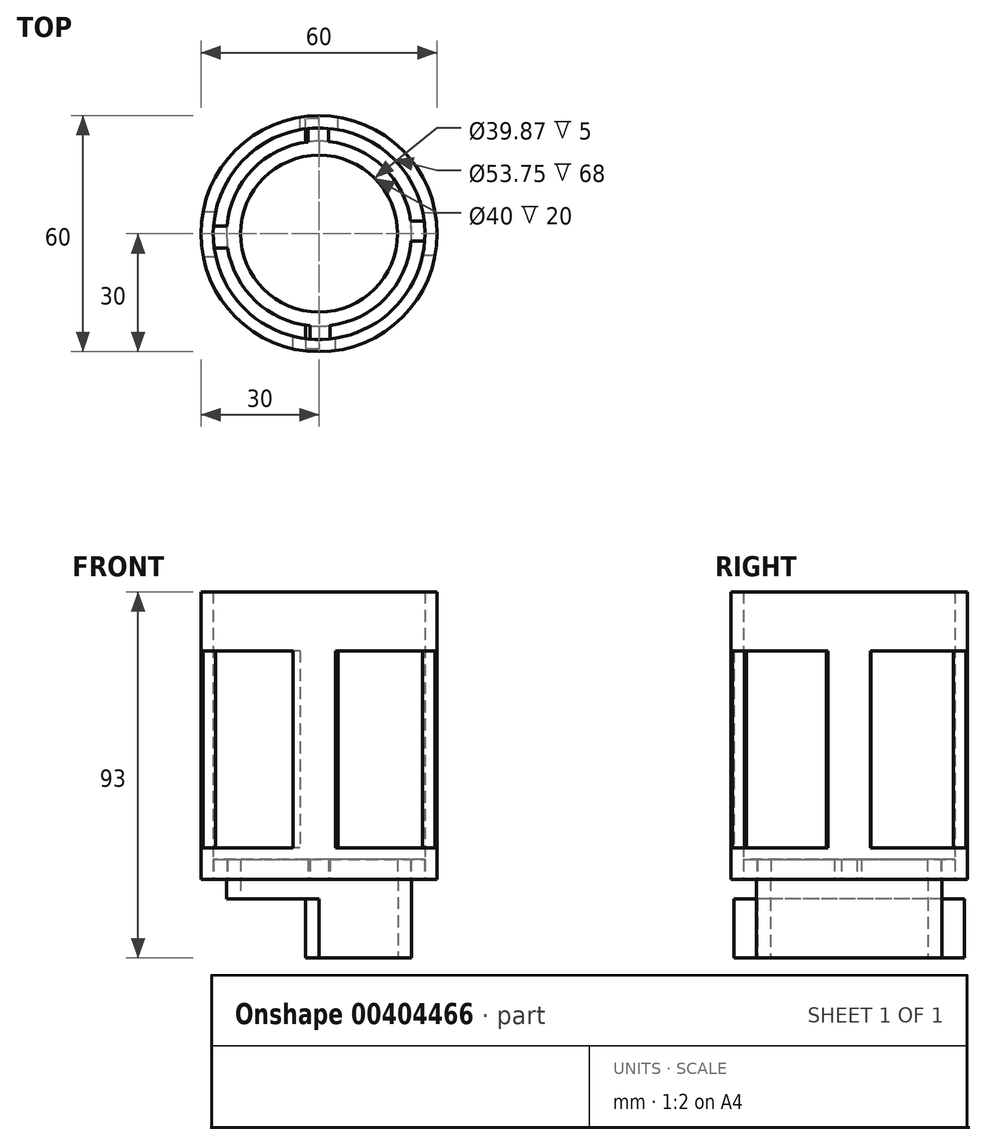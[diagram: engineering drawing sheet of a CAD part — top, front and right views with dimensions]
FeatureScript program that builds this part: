
annotation { "Feature Type Name" : "Feature", "Feature Type Description" : "" }
export const myFeature = defineFeature(function(context is Context, id is Id, definition is map)
    precondition{}
    {
        {
            var Q0;
            Q0=qCreatedBy(makeId("Top.planeOp"),FACE);
            var sketch = newSketch(context, id + "F0", { "sketchPlane" : qUnion([Q0])});
            skCircle(sketch, "E0", {"center": v(0, 0) * mm, "radius": 20 * mm});
            skCircle(sketch, "E1", {"center": v(0, 0) * mm, "radius": 23.5 * mm});
            skLineSegment(sketch, "E2", {"start": v(0, 23.5) * mm, "end": v(0, -23.5) * mm});
            skLineSegment(sketch, "E3", {"start": v(0, -23.5) * mm, "end": v(0, -29.3) * mm});
            skLineSegment(sketch, "E4", {"start": v(0, -29.3) * mm, "end": v(-3.38, -29.3) * mm});
            skLineSegment(sketch, "E5", {"start": v(-3.38, -23.26) * mm, "end": v(-3.38, -29.3) * mm});
            skLineSegment(sketch, "E6", {"start": v(0, 23.5) * mm, "end": v(0, 29.3) * mm});
            skLineSegment(sketch, "E7", {"start": v(0, 29.3) * mm, "end": v(-3.38, 29.3) * mm});
            skLineSegment(sketch, "E8", {"start": v(-3.38, 23.26) * mm, "end": v(-3.38, 29.3) * mm});
            skSolve(sketch);
        }
        {
            var Q0;
            {var subQ0=sQuery(id+"F0.wireOp",EDGE,"E2");var subQ1=sQuery(id+"F0.wireOp",EDGE,"E0");var subQ2=makeQuery(id+"F0.imprint","INTERSECT",VERTEX,{"disambiguationData":[OD(0.0)],"derivedFrom":[subQ1,subQ0]});Q0=makeQuery(id+"F0.imprint","IMPRINT",FACE,{"disambiguationData":[TD([[makeQuery(id+"F0.imprint","IMPRINT",EDGE,{"disambiguationData":[TD([[subQ2,-1.0]])],"derivedFrom":subQ1}),-1.0]])]});}
            var Q1;
            {var subQ0=sQuery(id+"F0.wireOp",EDGE,"E2");var subQ1=sQuery(id+"F0.wireOp",EDGE,"E0");var subQ2=makeQuery(id+"F0.imprint","INTERSECT",VERTEX,{"disambiguationData":[OD(0.0)],"derivedFrom":[subQ1,subQ0]});Q1=makeQuery(id+"F0.imprint","IMPRINT",FACE,{"disambiguationData":[TD([[makeQuery(id+"F0.imprint","IMPRINT",EDGE,{"disambiguationData":[TD([[subQ2,1.0]])],"derivedFrom":subQ1}),-1.0]])]});}
            extrude(context, id + "F1", {"entities" : qUnion([Q0, Q1]), "depth" : 20 * mm});
        }
        {
            var Q0;
            Q0=makeQuery(id+"F1.opExtrude","CAP_FACE",FACE,{"disambiguationData":[OSD([sQuery(id+"F0.wireOp",EDGE,"E0"),sQuery(id+"F0.wireOp",EDGE,"E1")])],"isStart":false});
            cPlane(context, id + "F2", {"entities" : qUnion([Q0]), "cplaneType" : CPlaneType.OFFSET, "offset" : 0 * mm, "width" : 152.4 * mm, "height" : 152.4 * mm});
        }
        {
            var Q0;
            Q0=qCreatedBy(id+"F2.planeOp",FACE);
            var sketch = newSketch(context, id + "F3", { "sketchPlane" : qUnion([Q0])});
            skArc(sketch, "E9", {"start": v(26.82, 3.15) * mm, "mid": v(18.84, 19.35) * mm, "end": v(2.44, 26.89) * mm});
            skCircle(sketch, "E10", {"center": v(0, 0) * mm, "radius": 30 * mm});
            skLineSegment(sketch, "E11", {"start": v(-2.35, -26.9) * mm, "end": v(-2.35, -23.38) * mm});
            skLineSegment(sketch, "E12", {"start": v(2.75, -26.86) * mm, "end": v(2.75, -23.34) * mm});
            skLineSegment(sketch, "E13", {"start": v(2.44, 26.89) * mm, "end": v(2.44, 23.37) * mm});
            skLineSegment(sketch, "E14", {"start": v(-2.85, 26.85) * mm, "end": v(-2.85, 23.33) * mm});
            skLineSegment(sketch, "E15", {"start": v(26.82, 3.15) * mm, "end": v(23.29, 3.15) * mm});
            skLineSegment(sketch, "E16", {"start": v(26.93, -1.94) * mm, "end": v(23.42, -1.94) * mm});
            skLineSegment(sketch, "E17", {"start": v(-26.75, -3.7) * mm, "end": v(-23.2, -3.7) * mm});
            skLineSegment(sketch, "E18", {"start": v(-26.93, 1.98) * mm, "end": v(-23.42, 1.98) * mm});
            skPoint(sketch, "E19", {"position": v(24.03, -12.3) * mm});
            skPoint(sketch, "E20", {"position": v(26.72, -13.65) * mm});
            skCircle(sketch, "E21", {"center": v(0, 0) * mm, "radius": 19.93 * mm});
            skArc(sketch, "E22.trimOffspring", {"start": v(-2.85, 26.85) * mm, "mid": v(-19.4, 18.78) * mm, "end": v(-26.93, 1.98) * mm});
            skArc(sketch, "E23.trimOffspring", {"start": v(-26.75, -3.7) * mm, "mid": v(-18.6, -19.57) * mm, "end": v(-2.35, -26.9) * mm});
            skArc(sketch, "E24.trimOffspring", {"start": v(2.75, -26.86) * mm, "mid": v(19.38, -18.8) * mm, "end": v(26.93, -1.94) * mm});
            skPoint(sketch, "E25", {"position": v(15.2, -17.37) * mm});
            skPoint(sketch, "E26", {"position": v(17.96, -20.16) * mm});
            skArc(sketch, "E27", {"start": v(-2.85, 23.33) * mm, "mid": v(-16.92, 16.3) * mm, "end": v(-23.42, 1.98) * mm});
            skArc(sketch, "E28.trimOffspring", {"start": v(23.29, 3.15) * mm, "mid": v(16.36, 16.87) * mm, "end": v(2.44, 23.37) * mm});
            skArc(sketch, "E29.trimOffspring", {"start": v(2.75, -23.34) * mm, "mid": v(16.9, -16.33) * mm, "end": v(23.42, -1.94) * mm});
            skArc(sketch, "E30.trimOffspring", {"start": v(-23.2, -3.7) * mm, "mid": v(-16.13, -17.1) * mm, "end": v(-2.35, -23.38) * mm});
            skSolve(sketch);
        }
        {
            var Q0;
            Q0=makeQuery(id+"F3.imprint","IMPRINT",FACE,{"disambiguationData":[TD([[makeQuery(id+"F3.imprint","IMPRINT",EDGE,{"derivedFrom":sQuery(id+"F3.wireOp",EDGE,"E9")}),-1.0]])]});
            extrude(context, id + "F4", {"entities" : qUnion([Q0]), "depth" : 5 * mm});
        }
        {
            var Q0;
            Q0=makeQuery(id+"F4.opExtrude","CAP_FACE",FACE,{"disambiguationData":[OSD([sQuery(id+"F3.wireOp",EDGE,"E9"),sQuery(id+"F3.wireOp",EDGE,"E10"),sQuery(id+"F3.wireOp",EDGE,"E11"),sQuery(id+"F3.wireOp",EDGE,"E12"),sQuery(id+"F3.wireOp",EDGE,"E13"),sQuery(id+"F3.wireOp",EDGE,"E14"),sQuery(id+"F3.wireOp",EDGE,"E15"),sQuery(id+"F3.wireOp",EDGE,"E16"),sQuery(id+"F3.wireOp",EDGE,"E17"),sQuery(id+"F3.wireOp",EDGE,"E18"),sQuery(id+"F3.wireOp",EDGE,"E21"),sQuery(id+"F3.wireOp",EDGE,"E22.trimOffspring"),sQuery(id+"F3.wireOp",EDGE,"E23.trimOffspring"),sQuery(id+"F3.wireOp",EDGE,"E24.trimOffspring"),sQuery(id+"F3.wireOp",EDGE,"E27"),sQuery(id+"F3.wireOp",EDGE,"E28.trimOffspring"),sQuery(id+"F3.wireOp",EDGE,"E29.trimOffspring"),sQuery(id+"F3.wireOp",EDGE,"E30.trimOffspring")])],"isStart":false});
            cPlane(context, id + "F5", {"entities" : qUnion([Q0]), "cplaneType" : CPlaneType.OFFSET, "offset" : 0 * mm, "width" : 152.4 * mm, "height" : 152.4 * mm});
        }
        {
            var Q0;
            Q0=qCreatedBy(id+"F5.planeOp",FACE);
            var sketch = newSketch(context, id + "F6", { "sketchPlane" : qUnion([Q0])});
            skCircle(sketch, "E31", {"center": v(0, 0) * mm, "radius": 26.87 * mm});
            skCircle(sketch, "E32", {"center": v(0, 0) * mm, "radius": 30 * mm});
            skSolve(sketch);
        }
        {
            var Q0;
            Q0=makeQuery(id+"F6.imprint","IMPRINT",FACE,{"disambiguationData":[TD([[makeQuery(id+"F6.imprint","IMPRINT",EDGE,{"derivedFrom":sQuery(id+"F6.wireOp",EDGE,"E31")}),-1.0]])]});
            extrude(context, id + "F7", {"entities" : qUnion([Q0]), "operationType" : NewBodyOperationType.ADD, "depth" : 3 * mm});
        }
        {
            var Q0;
            Q0=makeQuery(id+"F7.opExtrude","CAP_FACE",FACE,{"disambiguationData":[OSD([sQuery(id+"F6.wireOp",EDGE,"E31"),sQuery(id+"F6.wireOp",EDGE,"E32")])],"isStart":false});
            cPlane(context, id + "F8", {"entities" : qUnion([Q0]), "cplaneType" : CPlaneType.OFFSET, "offset" : 0 * mm, "width" : 152.4 * mm, "height" : 152.4 * mm});
        }
        {
            var Q0;
            Q0=qCreatedBy(id+"F8.planeOp",FACE);
            var sketch = newSketch(context, id + "F9", { "sketchPlane" : qUnion([Q0])});
            skLineSegment(sketch, "E33", {"start": v(-29.44, -5.78) * mm, "end": v(-26.24, -5.78) * mm});
            skLineSegment(sketch, "E34", {"start": v(-26.3, 5.53) * mm, "end": v(-29.49, 5.53) * mm});
            skLineSegment(sketch, "E35", {"start": v(-6.57, -29.27) * mm, "end": v(-6.57, -26.06) * mm});
            skLineSegment(sketch, "E36", {"start": v(4.14, -29.71) * mm, "end": v(4.14, -26.55) * mm});
            skLineSegment(sketch, "E37", {"start": v(26.32, -5.41) * mm, "end": v(29.5, -5.41) * mm});
            skLineSegment(sketch, "E38", {"start": v(26.32, 5.41) * mm, "end": v(29.5, 5.41) * mm});
            skLineSegment(sketch, "E39", {"start": v(-4.78, 26.44) * mm, "end": v(-4.78, 29.62) * mm});
            skLineSegment(sketch, "E40", {"start": v(4.83, 26.44) * mm, "end": v(4.83, 29.6) * mm});
            skArc(sketch, "E41", {"start": v(26.32, -5.41) * mm, "mid": v(26.87, 0) * mm, "end": v(26.32, 5.41) * mm});
            skArc(sketch, "E42", {"start": v(29.5, -5.41) * mm, "mid": v(30, 0) * mm, "end": v(29.5, 5.41) * mm});
            skArc(sketch, "E43.trimOffspring", {"start": v(-6.57, -26.06) * mm, "mid": v(-1.24, -26.84) * mm, "end": v(4.14, -26.55) * mm});
            skArc(sketch, "E44.trimOffspring", {"start": v(-26.3, 5.53) * mm, "mid": v(-26.87, -0.13) * mm, "end": v(-26.24, -5.78) * mm});
            skArc(sketch, "E45.trimOffspring", {"start": v(4.83, 26.44) * mm, "mid": v(0.02, 26.87) * mm, "end": v(-4.78, 26.44) * mm});
            skArc(sketch, "E46.trimOffspring", {"start": v(4.83, 29.6) * mm, "mid": v(0.02, 30) * mm, "end": v(-4.78, 29.62) * mm});
            skArc(sketch, "E47.trimOffspring", {"start": v(-29.49, 5.53) * mm, "mid": v(-30, -0.13) * mm, "end": v(-29.44, -5.78) * mm});
            skArc(sketch, "E48.trimOffspring", {"start": v(-6.57, -29.27) * mm, "mid": v(-1.23, -29.97) * mm, "end": v(4.14, -29.71) * mm});
            skSolve(sketch);
        }
        {
            var Q0;
            Q0=makeQuery(id+"F9.imprint","IMPRINT",FACE,{"disambiguationData":[TD([[makeQuery(id+"F9.imprint","IMPRINT",EDGE,{"derivedFrom":sQuery(id+"F9.wireOp",EDGE,"E37")}),1.0]])]});
            var Q1;
            Q1=makeQuery(id+"F9.imprint","IMPRINT",FACE,{"disambiguationData":[TD([[makeQuery(id+"F9.imprint","IMPRINT",EDGE,{"derivedFrom":sQuery(id+"F9.wireOp",EDGE,"E39")}),-1.0]])]});
            var Q2;
            Q2=makeQuery(id+"F9.imprint","IMPRINT",FACE,{"disambiguationData":[TD([[makeQuery(id+"F9.imprint","IMPRINT",EDGE,{"derivedFrom":sQuery(id+"F9.wireOp",EDGE,"E33")}),1.0]])]});
            var Q3;
            Q3=makeQuery(id+"F9.imprint","IMPRINT",FACE,{"disambiguationData":[TD([[makeQuery(id+"F9.imprint","IMPRINT",EDGE,{"derivedFrom":sQuery(id+"F9.wireOp",EDGE,"E35")}),-1.0]])]});
            extrude(context, id + "F10", {"entities" : qUnion([Q0, Q1, Q2, Q3]), "operationType" : NewBodyOperationType.ADD, "depth" : 50 * mm});
        }
        {
            var Q0;
            {var subQ0=sQuery(id+"F0.wireOp",EDGE,"E2");var subQ1=sQuery(id+"F0.wireOp",EDGE,"E0");var subQ2=makeQuery(id+"F0.imprint","INTERSECT",VERTEX,{"disambiguationData":[OD(0.0)],"derivedFrom":[subQ1,subQ0]});Q0=makeQuery(id+"F0.imprint","IMPRINT",FACE,{"disambiguationData":[TD([[makeQuery(id+"F0.imprint","IMPRINT",EDGE,{"disambiguationData":[TD([[subQ2,1.0]])],"derivedFrom":subQ1}),-1.0]])]});}
            extrude(context, id + "F11", {"entities" : qUnion([Q0]), "operationType" : NewBodyOperationType.REMOVE, "depth" : 15 * mm});
        }
        {
            var Q0;
            {var subQ0=sQuery(id+"F0.wireOp",EDGE,"E3");Q0=makeQuery(id+"F0.imprint","IMPRINT",FACE,{"disambiguationData":[TD([[makeQuery(id+"F0.imprint","IMPRINT",EDGE,{"derivedFrom":subQ0}),-1.0]])]});}
            var Q1;
            {var subQ0=sQuery(id+"F0.wireOp",EDGE,"E6");Q1=makeQuery(id+"F0.imprint","IMPRINT",FACE,{"disambiguationData":[TD([[makeQuery(id+"F0.imprint","IMPRINT",EDGE,{"derivedFrom":subQ0}),1.0]])]});}
            extrude(context, id + "F12", {"entities" : qUnion([Q0, Q1]), "operationType" : NewBodyOperationType.ADD, "depth" : 15 * mm});
        }
        {
            var Q0;
            Q0=makeQuery(id+"F10.opExtrude","CAP_FACE",FACE,{"disambiguationData":[OSD([sQuery(id+"F9.wireOp",EDGE,"E33"),sQuery(id+"F9.wireOp",EDGE,"E34"),sQuery(id+"F9.wireOp",EDGE,"E44.trimOffspring"),sQuery(id+"F9.wireOp",EDGE,"E47.trimOffspring")])],"isStart":false});
            cPlane(context, id + "F13", {"entities" : qUnion([Q0]), "cplaneType" : CPlaneType.OFFSET, "offset" : 0 * mm, "width" : 152.4 * mm, "height" : 152.4 * mm});
        }
        {
            var Q0;
            Q0=qCreatedBy(id+"F13.planeOp",FACE);
            var sketch = newSketch(context, id + "F14", { "sketchPlane" : qUnion([Q0])});
            skCircle(sketch, "E49", {"center": v(0, 0) * mm, "radius": 26.87 * mm});
            skCircle(sketch, "E50", {"center": v(0, 0) * mm, "radius": 30 * mm});
            skSolve(sketch);
        }
        {
            var Q0;
            Q0=makeQuery(id+"F14.imprint","IMPRINT",FACE,{"disambiguationData":[TD([[makeQuery(id+"F14.imprint","IMPRINT",EDGE,{"derivedFrom":sQuery(id+"F14.wireOp",EDGE,"E49")}),-1.0]])]});
            extrude(context, id + "F15", {"entities" : qUnion([Q0]), "operationType" : NewBodyOperationType.ADD, "depth" : 15 * mm});
        }
    });
